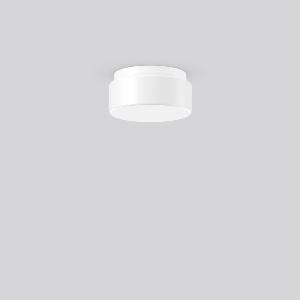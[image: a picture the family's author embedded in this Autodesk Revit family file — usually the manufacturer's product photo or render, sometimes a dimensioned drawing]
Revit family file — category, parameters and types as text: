
# Revit family: kreis_21101_002_17fb
name_source: partatom
category: Lighting Fixtures
units: mm (PartAtom-declared; Revit-internal decimal feet)

## family parameters
Cut with Voids When Loaded = No
Host = Face
Light Source = No
Part Type = Normal
Room Calculation Point = No
Round Connector Dimension = Use Diameter
Shared = No

## types (1)
- KREIS (1 x QA60/clear E27, 915 lm, 57 W, 3000)
    Apparent Load = 57 VA
    CIE Flux Codes = 34 63 85 71 62
    Color Rendering = 90
    Color Temperature = 3000
    Default Elevation = 1800 mm
    Description = Series: KREIS
Round surface-mounted luminaire in classic design. Base: plastic. Opal glass: mouth-blown, satin finish. Diffuser fastening: spring system. Suitable for Ceiling mounting, Wall (surface). IP 43 ceiling mounting, IP 44 wall mounting. 
Colour: white
Diameter: 230 mm
Height: 110 mm
Lamp: A60
Number of lamps: 1
Wattage: 75 W
Socket: E27
System power: 57 W
Rated luminous flux: 570 lm
Luminous efficiency: 10 lm/W
Control gear: Converter not necessary
Protection class: II
Type of protection: IP 43
    Height = 110 mm
    Lamp = 1 x QA60/clear E27
    Lamp Light Flux = 915 lm
    Lamp Power = 57 W
    Lamp count = 1
    Length = 230 mm
    Lifetime = 3000 h
    Luminous efficacy = 10 lm/W
    Manufacturer = RZB
    ModVariant = No
    Model = 21101.002
    Mounting Place = Ceiling, Wall
    Mounting Type = Surface mounted
    Number of Poles = 1
    OnlyDefault = Yes
    Power Factor = 1
    Product Name = KREIS
    Product group = Surface mounted ceiling and wall luminaires
    ProductGroupID = 305
    Protection Class = Protection class II
    Protection Degree = IP 43
    RLX_Detail_Level = 1
    RLX_Emergency_Light_Flux = 0 lm
    RLX_Emergency_Type = 0
    RLX_Emergency_Type_DB = No
    RlxData = <blob elided: 11133 chars, md5=64ebb9df>
    Socket = E27
    Standby Power = 0 W
    System Light Flux = 565 lm
    System Power = 57 W
    Type Comments = Product without accessories
    Type Image = 21101.002.jpg
    URL = http://relux.com
    VarID = ---
    Voltage = 230 V
    Voltage Range = 220-240 V
    Weight = 0.00 kg
    Width = 0 mm  [stored 0 ft]

note: [stored X ft] marks values corroborated as IEEE doubles in the binary element streams (Revit-internal decimal feet)

## geometry (parser evidence)
native form markers: Sweep x12
no freeform markers — native parametric forms only
